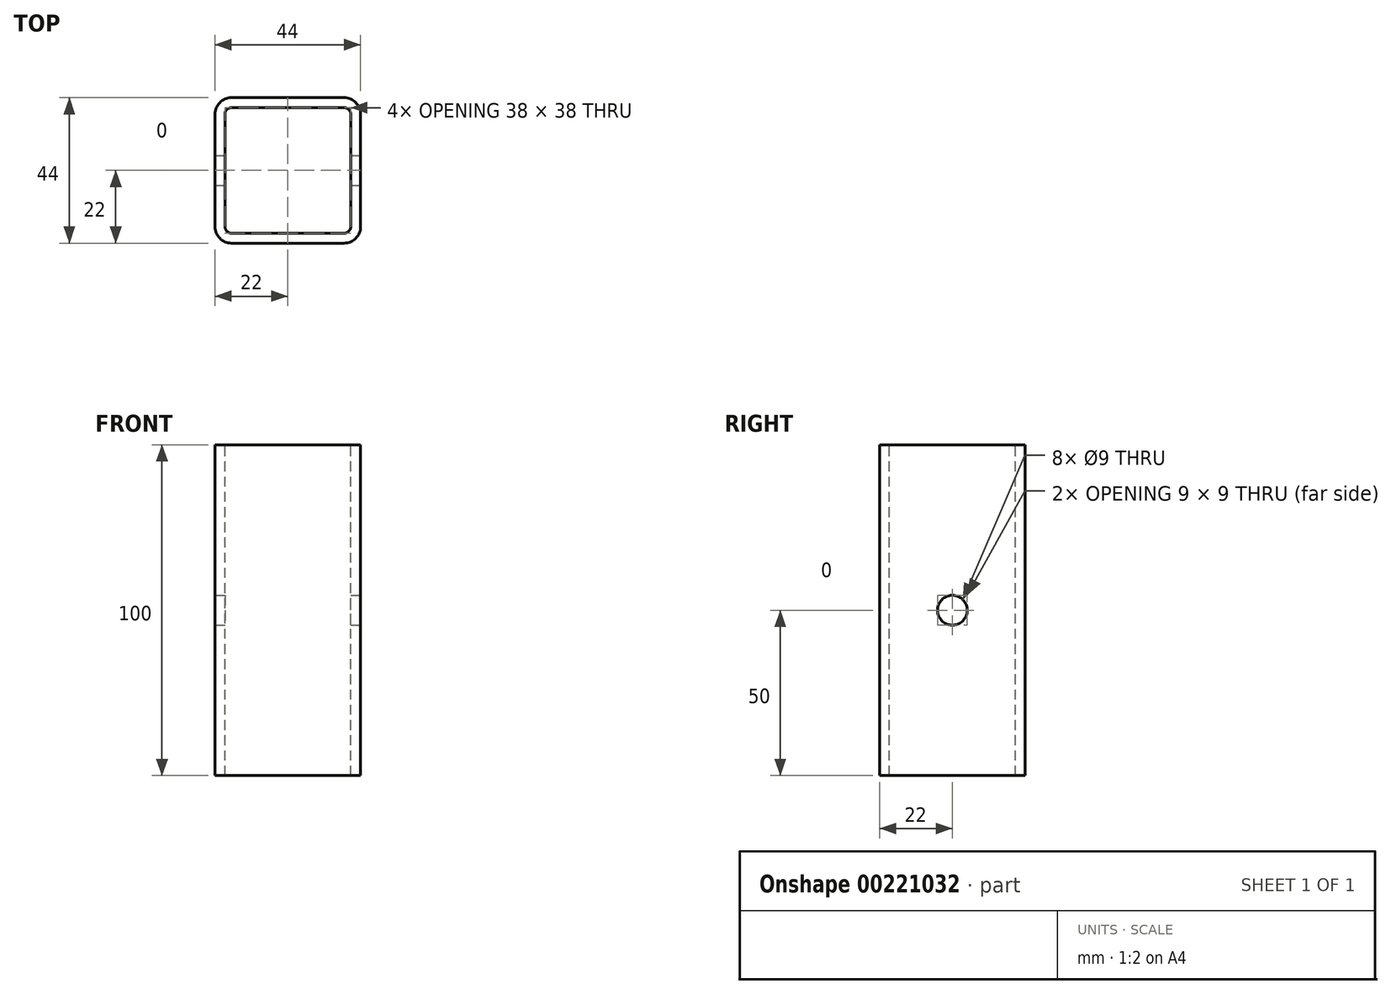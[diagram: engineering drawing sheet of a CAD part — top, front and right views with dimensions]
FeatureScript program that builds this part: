
annotation { "Feature Type Name" : "Feature", "Feature Type Description" : "" }
export const myFeature = defineFeature(function(context is Context, id is Id, definition is map)
    precondition{}
    {
        {
            var Q0;
            Q0=qCreatedBy(makeId("Top.planeOp"),FACE);
            var sketch = newSketch(context, id + "F0", { "sketchPlane" : qUnion([Q0])});
            skLineSegment(sketch, "E0.bottom", {"start": v(17, 22) * mm, "end": v(-17, 22) * mm});
            skLineSegment(sketch, "E0.top", {"start": v(17, -22) * mm, "end": v(-17, -22) * mm});
            skLineSegment(sketch, "E0.left", {"start": v(22, 17) * mm, "end": v(22, -17) * mm});
            skLineSegment(sketch, "E0.right", {"start": v(-22, 17) * mm, "end": v(-22, -17) * mm});
            skPoint(sketch, "E0.middle", {"position": v(0, 0) * mm});
            skPoint(sketch, "E1.visualSharp", {"position": v(22, -22) * mm});
            skArc(sketch, "E1.filletArc", {"start": v(17, -22) * mm, "mid": v(20.54, -20.54) * mm, "end": v(22, -17) * mm});
            skPoint(sketch, "E2.visualSharp", {"position": v(-22, -22) * mm});
            skArc(sketch, "E2.filletArc", {"start": v(-22, -17) * mm, "mid": v(-20.54, -20.54) * mm, "end": v(-17, -22) * mm});
            skPoint(sketch, "E3.visualSharp", {"position": v(-22, 22) * mm});
            skArc(sketch, "E3.filletArc", {"start": v(-17, 22) * mm, "mid": v(-20.54, 20.54) * mm, "end": v(-22, 17) * mm});
            skPoint(sketch, "E4.visualSharp", {"position": v(22, 22) * mm});
            skArc(sketch, "E4.filletArc", {"start": v(22, 17) * mm, "mid": v(20.54, 20.54) * mm, "end": v(17, 22) * mm});
            skSolve(sketch);
        }
        {
            var Q0;
            Q0=makeQuery(id+"F0.imprint","IMPRINT",FACE,{"disambiguationData":[TD([[makeQuery(id+"F0.imprint","IMPRINT",EDGE,{"derivedFrom":sQuery(id+"F0.wireOp",EDGE,"E0.bottom")}),1.0]])]});
            extrude(context, id + "F1", {"entities" : qUnion([Q0]), "depth" : 100 * mm});
        }
        {
            var Q0;
            Q0=makeQuery(id+"F1.opExtrude","CAP_FACE",FACE,{"disambiguationData":[OSD([sQuery(id+"F0.wireOp",EDGE,"E0.bottom"),sQuery(id+"F0.wireOp",EDGE,"E0.top"),sQuery(id+"F0.wireOp",EDGE,"E0.left"),sQuery(id+"F0.wireOp",EDGE,"E0.right"),sQuery(id+"F0.wireOp",EDGE,"E1.filletArc"),sQuery(id+"F0.wireOp",EDGE,"E2.filletArc"),sQuery(id+"F0.wireOp",EDGE,"E3.filletArc"),sQuery(id+"F0.wireOp",EDGE,"E4.filletArc")])],"isStart":false});
            var sketch = newSketch(context, id + "F2", { "sketchPlane" : qUnion([Q0])});
            skLineSegment(sketch, "E5.0", {"start": v(-17, -19) * mm, "end": v(17, -19) * mm});
            skLineSegment(sketch, "E5.1", {"start": v(-19, 17) * mm, "end": v(-19, -17) * mm});
            skLineSegment(sketch, "E5.2", {"start": v(17, 19) * mm, "end": v(-17, 19) * mm});
            skLineSegment(sketch, "E5.3", {"start": v(19, -17) * mm, "end": v(19, 17) * mm});
            skPoint(sketch, "E6.visualSharp", {"position": v(-19, -19) * mm});
            skArc(sketch, "E6.filletArc", {"start": v(-19, -17) * mm, "mid": v(-18.41, -18.41) * mm, "end": v(-17, -19) * mm});
            skPoint(sketch, "E7.visualSharp", {"position": v(19, -19) * mm});
            skArc(sketch, "E7.filletArc", {"start": v(17, -19) * mm, "mid": v(18.41, -18.41) * mm, "end": v(19, -17) * mm});
            skPoint(sketch, "E8.visualSharp", {"position": v(19, 19) * mm});
            skArc(sketch, "E8.filletArc", {"start": v(19, 17) * mm, "mid": v(18.41, 18.41) * mm, "end": v(17, 19) * mm});
            skPoint(sketch, "E9.visualSharp", {"position": v(-19, 19) * mm});
            skArc(sketch, "E9.filletArc", {"start": v(-17, 19) * mm, "mid": v(-18.41, 18.41) * mm, "end": v(-19, 17) * mm});
            skSolve(sketch);
        }
        {
            var Q0;
            Q0=makeQuery(id+"F2.imprint","IMPRINT",FACE,{"disambiguationData":[TD([[makeQuery(id+"F2.imprint","IMPRINT",EDGE,{"derivedFrom":sQuery(id+"F2.wireOp",EDGE,"E5.0")}),1.0]])]});
            extrude(context, id + "F3", {"entities" : qUnion([Q0]), "operationType" : NewBodyOperationType.REMOVE, "endBound" : BoundingType.THROUGH_ALL, "oppositeDirection" : true, "depth" : 25 * mm});
        }
        {
            var Q0;
            Q0=makeQuery(id+"F1.opExtrude","SWEPT_FACE",FACE,{"disambiguationData":[OSD([sQuery(id+"F0.wireOp",EDGE,"E0.left")])]});
            var sketch = newSketch(context, id + "F4", { "sketchPlane" : qUnion([Q0])});
            skPoint(sketch, "E10", {"position": v(0, 50) * mm});
            skSolve(sketch);
        }
        {
            var Q0;
            Q0=sQuery(id+"F4.wireOp",VERTEX,"E10");
            var Q1;
            Q1=makeQuery(id+"F1.opExtrude","SWEPT_BODY",BODY,{"disambiguationData":[OSD([sQuery(id+"F0.wireOp",EDGE,"E0.bottom"),sQuery(id+"F0.wireOp",EDGE,"E0.top"),sQuery(id+"F0.wireOp",EDGE,"E0.left"),sQuery(id+"F0.wireOp",EDGE,"E0.right"),sQuery(id+"F0.wireOp",EDGE,"E1.filletArc"),sQuery(id+"F0.wireOp",EDGE,"E2.filletArc"),sQuery(id+"F0.wireOp",EDGE,"E3.filletArc"),sQuery(id+"F0.wireOp",EDGE,"E4.filletArc")])]});
            hole(context, id + "F5", {"style" : HoleStyle.SIMPLE, "endStyle" : HoleEndStyle.THROUGH, "holeDiameter" : 9 * mm, "locations" : qUnion([Q0]), "scope" : qUnion([Q1]), "isTappedThrough" : true});
        }
    });
